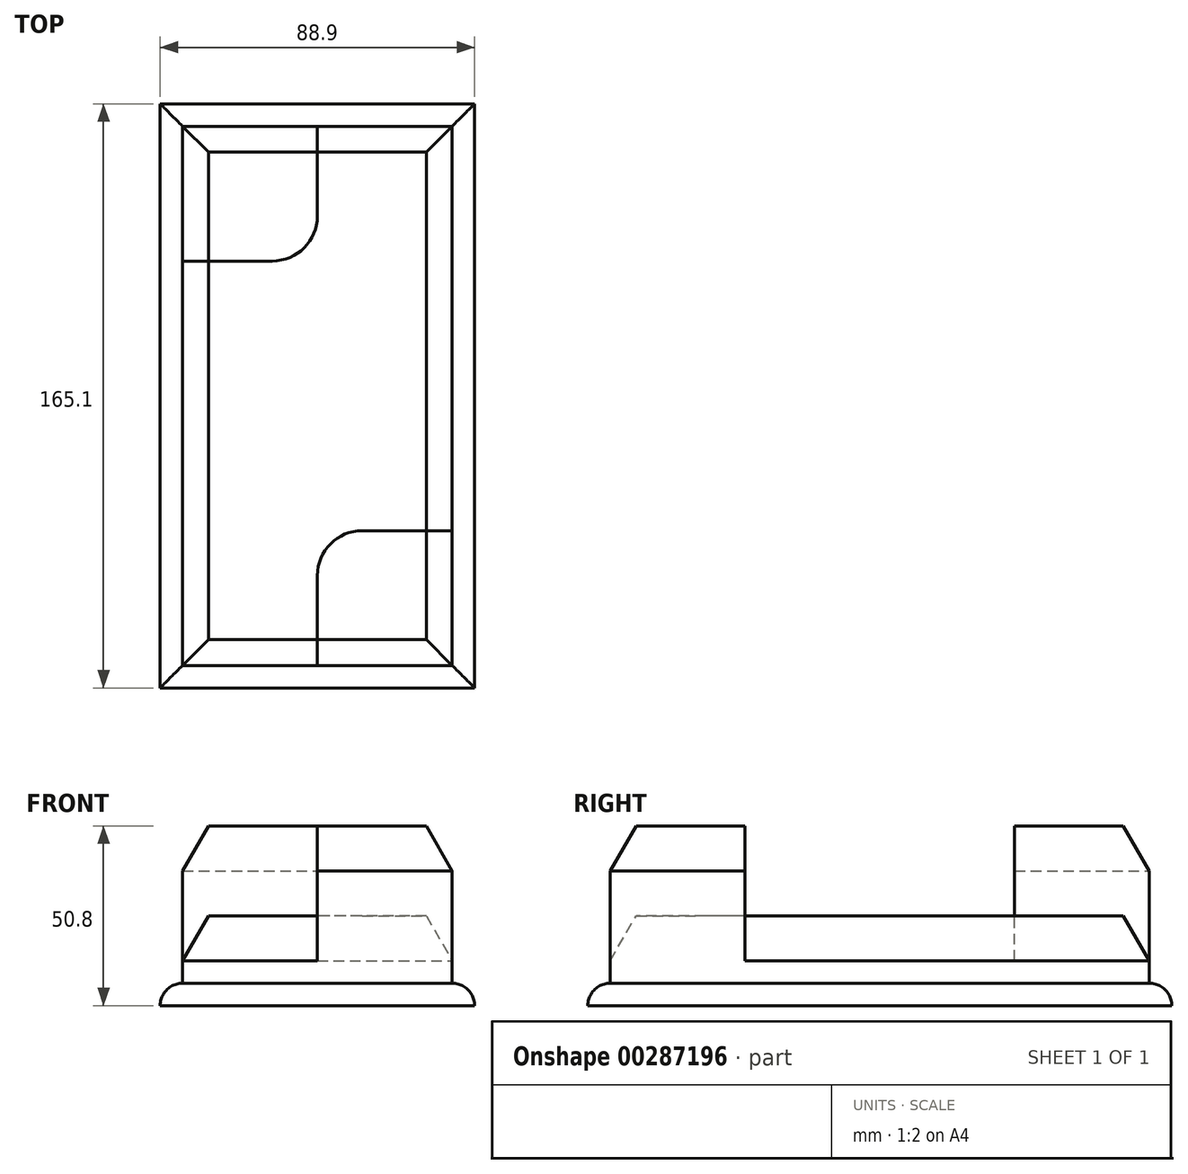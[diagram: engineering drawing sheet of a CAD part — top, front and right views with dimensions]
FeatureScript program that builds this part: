
annotation { "Feature Type Name" : "Feature", "Feature Type Description" : "" }
export const myFeature = defineFeature(function(context is Context, id is Id, definition is map)
    precondition{}
    {
        {
            var Q0;
            Q0=qCreatedBy(makeId("Top.planeOp"),FACE);
            var sketch = newSketch(context, id + "F0", { "sketchPlane" : qUnion([Q0])});
            skLineSegment(sketch, "E0.bottom", {"start": v(38.1, 76.2) * mm, "end": v(-38.1, 76.2) * mm});
            skLineSegment(sketch, "E0.top", {"start": v(38.1, -76.2) * mm, "end": v(-38.1, -76.2) * mm});
            skLineSegment(sketch, "E0.left", {"start": v(38.1, 76.2) * mm, "end": v(38.1, -76.2) * mm});
            skLineSegment(sketch, "E0.right", {"start": v(-38.1, 76.2) * mm, "end": v(-38.1, -76.2) * mm});
            skPoint(sketch, "E0.middle", {"position": v(0, 0) * mm});
            skLineSegment(sketch, "E1.0", {"start": v(-44.45, 82.55) * mm, "end": v(-44.45, -82.55) * mm});
            skLineSegment(sketch, "E1.1", {"start": v(44.45, 82.55) * mm, "end": v(-44.45, 82.55) * mm});
            skLineSegment(sketch, "E1.2", {"start": v(44.45, 82.55) * mm, "end": v(44.45, -82.55) * mm});
            skLineSegment(sketch, "E1.3", {"start": v(44.45, -82.55) * mm, "end": v(-44.45, -82.55) * mm});
            skLineSegment(sketch, "E2", {"start": v(0, 76.2) * mm, "end": v(0, 50.8) * mm});
            skLineSegment(sketch, "E3", {"start": v(-12.7, 38.1) * mm, "end": v(-38.1, 38.1) * mm});
            skLineSegment(sketch, "E4", {"start": v(0, -76.2) * mm, "end": v(0, -50.8) * mm});
            skPoint(sketch, "E4.endSnap0", {"position": v(0, -76.2) * mm});
            skLineSegment(sketch, "E5", {"start": v(12.7, -38.1) * mm, "end": v(38.1, -38.1) * mm});
            skPoint(sketch, "E6.visualSharp", {"position": v(0, 38.1) * mm});
            skArc(sketch, "E6.filletArc", {"start": v(-12.7, 38.1) * mm, "mid": v(-3.72, 41.82) * mm, "end": v(0, 50.8) * mm});
            skPoint(sketch, "E7.visualSharp", {"position": v(0, -38.1) * mm});
            skArc(sketch, "E7.filletArc", {"start": v(12.7, -38.1) * mm, "mid": v(3.72, -41.82) * mm, "end": v(0, -50.8) * mm});
            skSolve(sketch);
        }
        {
            var Q0;
            Q0 = qSketchRegion(id + "F0", true);
            extrude(context, id + "F1", {"entities" : qUnion([Q0]), "depth" : 6.35 * mm});
        }
        {
            var Q0;
            {var subQ9=sQuery(id+"F0.wireOp",EDGE,"E2");Q0=makeQuery(id+"F0.imprint","IMPRINT",FACE,{"disambiguationData":[TD([[makeQuery(id+"F0.imprint","IMPRINT",EDGE,{"derivedFrom":subQ9}),1.0]])]});}
            extrude(context, id + "F2", {"entities" : qUnion([Q0]), "operationType" : NewBodyOperationType.ADD, "depth" : 25.4 * mm});
        }
        {
            var Q0;
            {var subQ1=sQuery(id+"F0.wireOp",EDGE,"E2");Q0=makeQuery(id+"F0.imprint","IMPRINT",FACE,{"disambiguationData":[TD([[makeQuery(id+"F0.imprint","IMPRINT",EDGE,{"derivedFrom":subQ1}),-1.0]])]});}
            var Q1;
            {var subQ0=sQuery(id+"F0.wireOp",EDGE,"E4");Q1=makeQuery(id+"F0.imprint","IMPRINT",FACE,{"disambiguationData":[TD([[makeQuery(id+"F0.imprint","IMPRINT",EDGE,{"derivedFrom":subQ0}),-1.0]])]});}
            extrude(context, id + "F3", {"entities" : qUnion([Q0, Q1]), "operationType" : NewBodyOperationType.ADD, "depth" : 50.8 * mm});
        }
        {
            var Q0;
            Q0=makeQuery(id+"F1.opExtrude","CAP_EDGE",EDGE,{"disambiguationData":[OSD([sQuery(id+"F0.wireOp",EDGE,"E1.0")])],"isStart":false});
            var Q1;
            Q1=makeQuery(id+"F1.opExtrude","CAP_EDGE",EDGE,{"disambiguationData":[OSD([sQuery(id+"F0.wireOp",EDGE,"E1.3")])],"isStart":false});
            var Q2;
            Q2=makeQuery(id+"F1.opExtrude","CAP_EDGE",EDGE,{"disambiguationData":[OSD([sQuery(id+"F0.wireOp",EDGE,"E1.2")])],"isStart":false});
            var Q3;
            Q3=makeQuery(id+"F1.opExtrude","CAP_EDGE",EDGE,{"disambiguationData":[OSD([sQuery(id+"F0.wireOp",EDGE,"E1.1")])],"isStart":false});
            fillet(context, id + "F4", {"entities" : qUnion([Q0, Q1, Q2, Q3]), "radius" : 6.35 * mm, "tangentPropagation" : true, "allowEdgeOverflow" : false});
        }
        {
            var Q0;
            Q0=makeQuery(id+"F2.opExtrude","CAP_EDGE",EDGE,{"disambiguationData":[OSD([sQuery(id+"F0.wireOp",EDGE,"E0.left")])],"isStart":false});
            var Q1;
            Q1=makeQuery(id+"F2.opExtrude","CAP_EDGE",EDGE,{"disambiguationData":[OSD([sQuery(id+"F0.wireOp",EDGE,"E0.bottom")])],"isStart":false});
            var Q2;
            Q2=makeQuery(id+"F2.opExtrude","CAP_EDGE",EDGE,{"disambiguationData":[OSD([sQuery(id+"F0.wireOp",EDGE,"E0.right")])],"isStart":false});
            var Q3;
            Q3=makeQuery(id+"F2.opExtrude","CAP_EDGE",EDGE,{"disambiguationData":[OSD([sQuery(id+"F0.wireOp",EDGE,"E0.top")])],"isStart":false});
            var Q4;
            Q4=makeQuery(id+"F3.opExtrude","CAP_EDGE",EDGE,{"disambiguationData":[OSD([sQuery(id+"F0.wireOp",EDGE,"E0.top")])],"isStart":false});
            var Q5;
            Q5=makeQuery(id+"F3.opExtrude","CAP_EDGE",EDGE,{"disambiguationData":[OSD([sQuery(id+"F0.wireOp",EDGE,"E0.left")])],"isStart":false});
            chamfer(context, id + "F5", {"entities" : qUnion([Q0, Q1, Q2, Q3, Q4, Q5]), "chamferType" : ChamferType.OFFSET_ANGLE, "width" : 12.7 * mm, "oppositeDirection" : false, "angle" : 30 * degree, "tangentPropagation" : true});
        }
        {
            var Q0;
            Q0=makeQuery(id+"F3.opExtrude","CAP_EDGE",EDGE,{"disambiguationData":[OSD([sQuery(id+"F0.wireOp",EDGE,"E0.bottom")])],"isStart":false});
            var Q1;
            Q1=makeQuery(id+"F3.opExtrude","CAP_EDGE",EDGE,{"disambiguationData":[OSD([sQuery(id+"F0.wireOp",EDGE,"E0.right")])],"isStart":false});
            chamfer(context, id + "F6", {"entities" : qUnion([Q0, Q1]), "chamferType" : ChamferType.OFFSET_ANGLE, "width" : 12.7 * mm, "oppositeDirection" : true, "angle" : 30 * degree, "tangentPropagation" : true});
        }
    });
